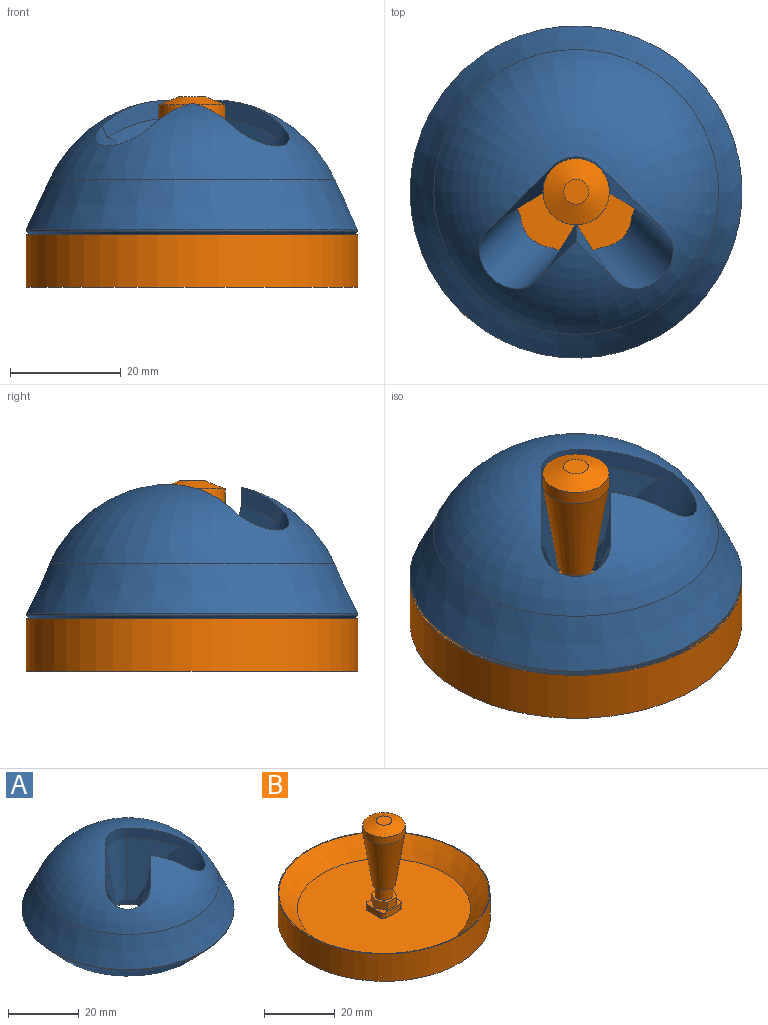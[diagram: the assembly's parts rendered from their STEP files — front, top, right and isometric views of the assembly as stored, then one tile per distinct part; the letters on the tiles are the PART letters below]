
ASSEMBLY  parts=2 mates=1
PART A: 21 faces, bbox 60x60x30.3 mm
  f0: torus R=3.07mm, axis (0,0,1), area 2277.5mm2, adj f3,f11,f12,f13,f15,f17,f18,f20
  f1: cone r=30mm half-angle=43.7deg, axis (0,0,1), area 1455.5mm2, adj f2,f4
  f2: cylinder r=30mm len=60mm, axis (0,0,-1), area 40.3mm2, adj f1,f3
  f3: cone r=30mm half-angle=25deg, axis (0,0,-1), area 1768.6mm2, adj f0,f2
  f4: plane 48.17x48.17mm, normal (0,0,-1), area 1434.3mm2, adj f1,f7,f8,f13,f18
  f5: cone r=36.77mm half-angle=82deg, axis (-0.71,-0.71,0), area 63.3mm2, adj f12,f13,f16
  f6: cone r=6.3mm half-angle=8deg, axis (0,0,1), area 153.3mm2, adj f10,f11,f14,f19
  f7: cylinder r=11mm len=9.13mm, axis (0,0,-1), area 29.4mm2, adj f4,f9,f13,f18
  f8: cylinder r=11mm len=22mm, axis (0,0,-1), area 184.9mm2, adj f4,f10,f13,f18
  f9: cone r=3mm half-angle=72.6deg, axis (0,0,-1), area 5.1mm2, adj f7,f13,f18
  f10: cone r=3mm half-angle=72.6deg, axis (0,0,-1), area 172.2mm2, adj f6,f8,f13,f14,f18,f19
  f11: cylinder r=6.3mm len=8.91mm, axis (0,0,-1), area 32.8mm2, adj f0,f6,f15,f20
  f12: plane 7.27x7.27mm, normal (0.71,0.71,0), area 31.4mm2, adj f0,f5,f13,f17
  f13: cylinder r=6.3mm len=28.01mm, axis (0.3,-0.3,0.91), area 610.3mm2, adj f0,f4,f5,f7,f8,f9,f10,f12
  f14: cone r=0mm half-angle=82deg, axis (0.71,0.71,0), area 160.3mm2, adj f6,f10,f13,f15
  f15: plane 11.73x11.73mm, normal (-0.71,-0.71,0), area 52.4mm2, adj f0,f11,f13,f14
  f16: cone r=36.77mm half-angle=82deg, axis (0.71,-0.71,0), area 63.3mm2, adj f5,f17,f18
  f17: plane 7.27x7.27mm, normal (-0.71,0.71,0), area 31.4mm2, adj f0,f12,f16,f18
  f18: cylinder r=6.3mm len=28.01mm, axis (-0.3,-0.3,0.91), area 610.3mm2, adj f0,f4,f7,f8,f9,f10,f13,f16
  f19: cone r=0mm half-angle=82deg, axis (-0.71,0.71,0), area 160.3mm2, adj f6,f10,f18,f20
  f20: plane 11.73x11.73mm, normal (0.71,-0.71,0), area 52.5mm2, adj f0,f11,f18,f19
PART B: 27 faces, bbox 60x60x34.5 mm
  f0: plane 8x7.5mm, normal (0,0,1), area 22.6mm2, adj f6,f7,f8,f9,f10,f11,f12,f13
  f1: plane 60x60mm, normal (0,0,-1), area 2827.4mm2, adj f2
  f2: cylinder r=30mm len=60mm, axis (0,0,-1), area 1790.7mm2, adj f1,f3
  f3: plane 60x60mm, normal (0,0,1), area 46.9mm2, adj f2,f4
  f4: cone r=24.5mm half-angle=43.7deg, axis (0,0,1), area 1295.9mm2, adj f3,f5
  f5: plane 49x49mm, normal (0,0,1), area 1826.6mm2, adj f4,f6,f7,f8,f9,f10,f11,f12
  f6: plane 6x2mm, normal (0,-1,0), area 12mm2, adj f0,f5,f10,f13
  f7: plane 5.5x2mm, normal (1,0,0), area 11mm2, adj f0,f5,f10,f11
  f8: plane 6x2mm, normal (0,1,0), area 12mm2, adj f0,f5,f11,f12
  f9: plane 5.5x2mm, normal (-1,0,0), area 11mm2, adj f0,f5,f12,f13
  f10: cylinder r=1mm len=2mm, axis (0,0,-1), area 3.1mm2, adj f0,f5,f6,f7
  f11: cylinder r=1mm len=2mm, axis (0,0,1), area 3.1mm2, adj f0,f5,f7,f8
  f12: cylinder r=1mm len=2mm, axis (0,0,-1), area 3.1mm2, adj f0,f5,f8,f9
  f13: cylinder r=1mm len=2mm, axis (0,0,1), area 3.1mm2, adj f0,f5,f6,f9
  f14: plane 3.25x2.7mm, normal (0.87,-0.5,0), area 10.1mm2, adj f0,f15,f19,f20
  f15: plane 3.25x2.7mm, normal (0.87,0.5,0), area 10.1mm2, adj f0,f14,f16,f20
  f16: plane 3.75x2.7mm, normal (0,1,0), area 10.1mm2, adj f0,f15,f17,f20
  f17: plane 3.25x2.7mm, normal (-0.87,0.5,0), area 10.1mm2, adj f0,f16,f18,f20
  f18: plane 3.25x2.7mm, normal (-0.87,-0.5,0), area 10.1mm2, adj f0,f17,f19,f20
  f19: plane 3.75x2.7mm, normal (0,-1,0), area 10.1mm2, adj f0,f14,f18,f20
  f20: plane 7.51x6.5mm, normal (0,0,1), area 17mm2, adj f14,f15,f16,f17,f18,f19,f21
  f21: cylinder r=2.5mm len=5mm, axis (0,0,-1), area 62.9mm2, adj f20,f22
  f22: plane 6.5x6.5mm, normal (0,0,-1), area 13.5mm2, adj f21,f23
  f23: cone r=6mm half-angle=8.8deg, axis (0,0,1), area 523.3mm2, adj f22,f24
  f24: cylinder r=6mm len=12mm, axis (0,0,-1), area 94.2mm2, adj f23,f25
  f25: cone r=2.25mm half-angle=68.2deg, axis (0,0,-1), area 104.7mm2, adj f24,f26
  f26: plane 4.5x4.5mm, normal (0,0,1), area 15.9mm2, adj f25
PLACE A at identity
PLACE B at identity fixed
MATE cylindrical B.f2 <-> A.f0  axis (0,0,1) through (0,0,0)mm
